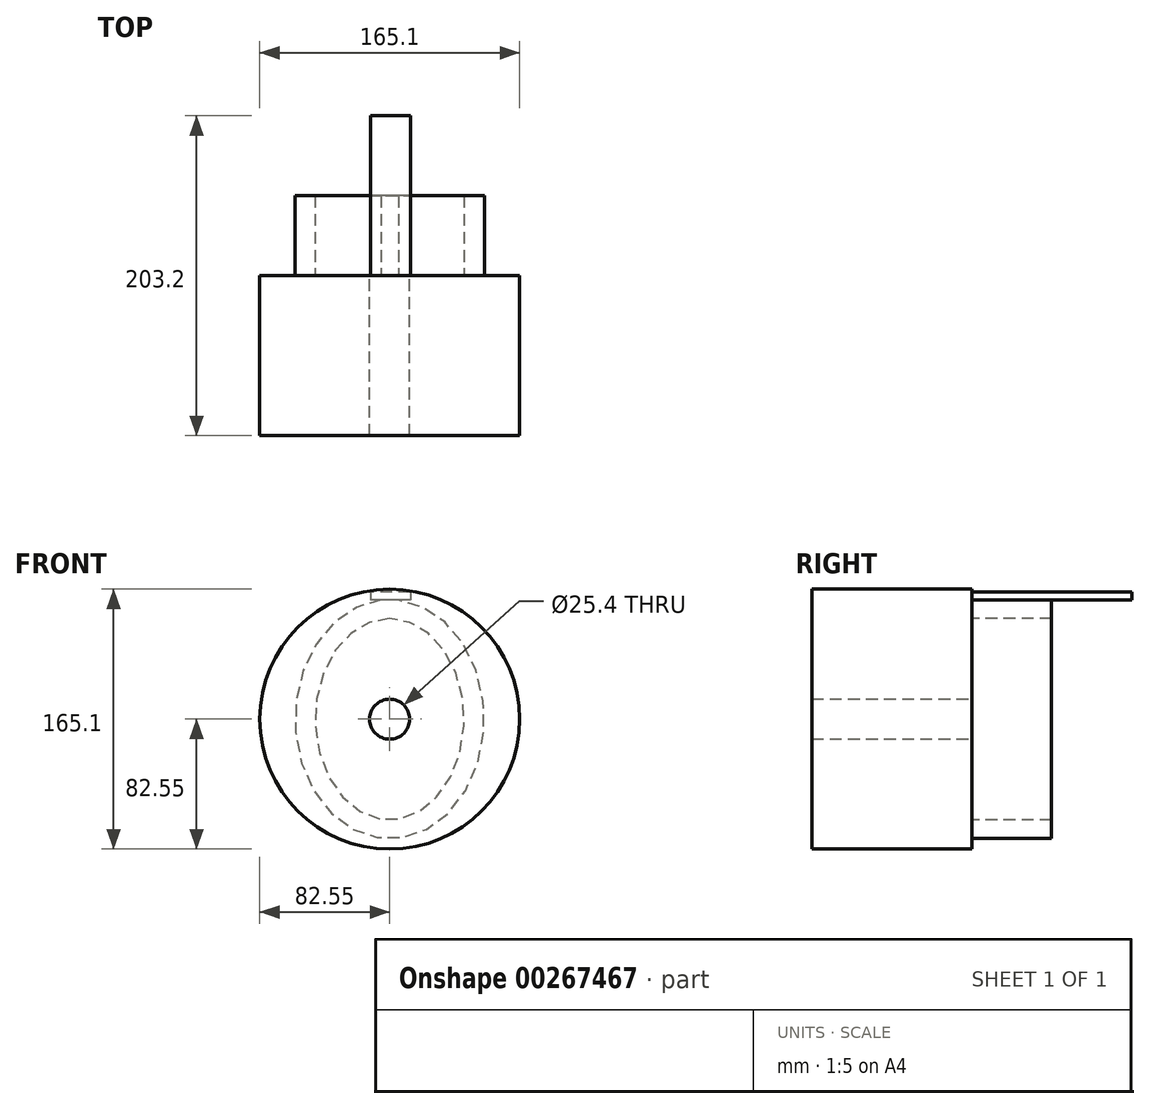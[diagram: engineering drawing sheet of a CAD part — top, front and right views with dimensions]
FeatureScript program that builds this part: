
annotation { "Feature Type Name" : "Feature", "Feature Type Description" : "" }
export const myFeature = defineFeature(function(context is Context, id is Id, definition is map)
    precondition{}
    {
        {
            var Q0;
            Q0=qCreatedBy(makeId("Front.planeOp"),FACE);
            var sketch = newSketch(context, id + "F0", { "sketchPlane" : qUnion([Q0])});
            skCircle(sketch, "E0", {"center": v(0, 0) * mm, "radius": 82.55 * mm});
            skSolve(sketch);
        }
        {
            var Q0;
            Q0=makeQuery(id+"F0.imprint","IMPRINT",FACE,{"disambiguationData":[TD([[makeQuery(id+"F0.imprint","IMPRINT",EDGE,{"derivedFrom":sQuery(id+"F0.wireOp",EDGE,"E0")}),1.0]])]});
            extrude(context, id + "F1", {"entities" : qUnion([Q0]), "depth" : 101.6 * mm});
        }
        {
            var Q0;
            Q0=qCreatedBy(makeId("Front.planeOp"),FACE);
            var sketch = newSketch(context, id + "F2", { "sketchPlane" : qUnion([Q0])});
            skEllipse(sketch, "E1", {"center": v(0, 0) * mm, "majorRadius": 75.87 * mm, "minorRadius": 60.1 * mm, "majorAxis": v(0, 1)});
            skSolve(sketch);
        }
        {
            var Q0;
            Q0=qCreatedBy(makeId("Front.planeOp"),FACE);
            var sketch = newSketch(context, id + "F3", { "sketchPlane" : qUnion([Q0])});
            skEllipse(sketch, "E2", {"center": v(0, 0) * mm, "majorRadius": 63.5 * mm, "minorRadius": 45.72 * mm, "majorAxis": v(0, 1)});
            skSolve(sketch);
        }
        {
            var Q0;
            Q0 = qSketchRegion(id + "F3", true);
            extrude(context, id + "F4", {"entities" : qUnion([Q0]), "operationType" : NewBodyOperationType.REMOVE, "oppositeDirection" : true, "depth" : 25.4 * mm});
        }
        {
            var Q0;
            Q0=makeQuery(id+"F2.imprint","IMPRINT",FACE,{"disambiguationData":[TD([[makeQuery(id+"F2.imprint","IMPRINT",EDGE,{"derivedFrom":sQuery(id+"F2.wireOp",EDGE,"E1")}),1.0]])]});
            extrude(context, id + "F5", {"entities" : qUnion([Q0]), "operationType" : NewBodyOperationType.ADD, "oppositeDirection" : true, "depth" : 50.8 * mm});
        }
        {
            var Q0;
            Q0=qCreatedBy(makeId("Front.planeOp"),FACE);
            var sketch = newSketch(context, id + "F6", { "sketchPlane" : qUnion([Q0])});
            skEllipse(sketch, "E3", {"center": v(0, 0) * mm, "majorRadius": 63.85 * mm, "minorRadius": 47.3 * mm, "majorAxis": v(0, 1)});
            skSolve(sketch);
        }
        {
            var Q0;
            Q0 = qSketchRegion(id + "F6", true);
            extrude(context, id + "F7", {"entities" : qUnion([Q0]), "operationType" : NewBodyOperationType.REMOVE, "oppositeDirection" : true, "depth" : 50.8 * mm});
        }
        {
            var Q0;
            Q0=qCreatedBy(makeId("Front.planeOp"),FACE);
            var sketch = newSketch(context, id + "F8", { "sketchPlane" : qUnion([Q0])});
            skLineSegment(sketch, "E4.bottom", {"start": v(13.13, 80.63) * mm, "end": v(-12.27, 80.63) * mm});
            skLineSegment(sketch, "E4.top", {"start": v(13.13, 75.55) * mm, "end": v(-12.27, 75.55) * mm});
            skLineSegment(sketch, "E4.left", {"start": v(13.13, 80.63) * mm, "end": v(13.13, 75.55) * mm});
            skLineSegment(sketch, "E4.right", {"start": v(-12.27, 80.63) * mm, "end": v(-12.27, 75.55) * mm});
            skSolve(sketch);
        }
        {
            var Q0;
            Q0 = qSketchRegion(id + "F8", true);
            extrude(context, id + "F9", {"entities" : qUnion([Q0]), "operationType" : NewBodyOperationType.ADD, "oppositeDirection" : true, "depth" : 101.6 * mm});
        }
        {
            var Q0;
            Q0=qCreatedBy(makeId("Front.planeOp"),FACE);
            var sketch = newSketch(context, id + "F10", { "sketchPlane" : qUnion([Q0])});
            skCircle(sketch, "E5", {"center": v(0, 0) * mm, "radius": 12.7 * mm});
            skSolve(sketch);
        }
        {
            var Q0;
            Q0 = qSketchRegion(id + "F10", true);
            extrude(context, id + "F11", {"entities" : qUnion([Q0]), "operationType" : NewBodyOperationType.REMOVE, "depth" : 101.6 * mm});
        }
    });
